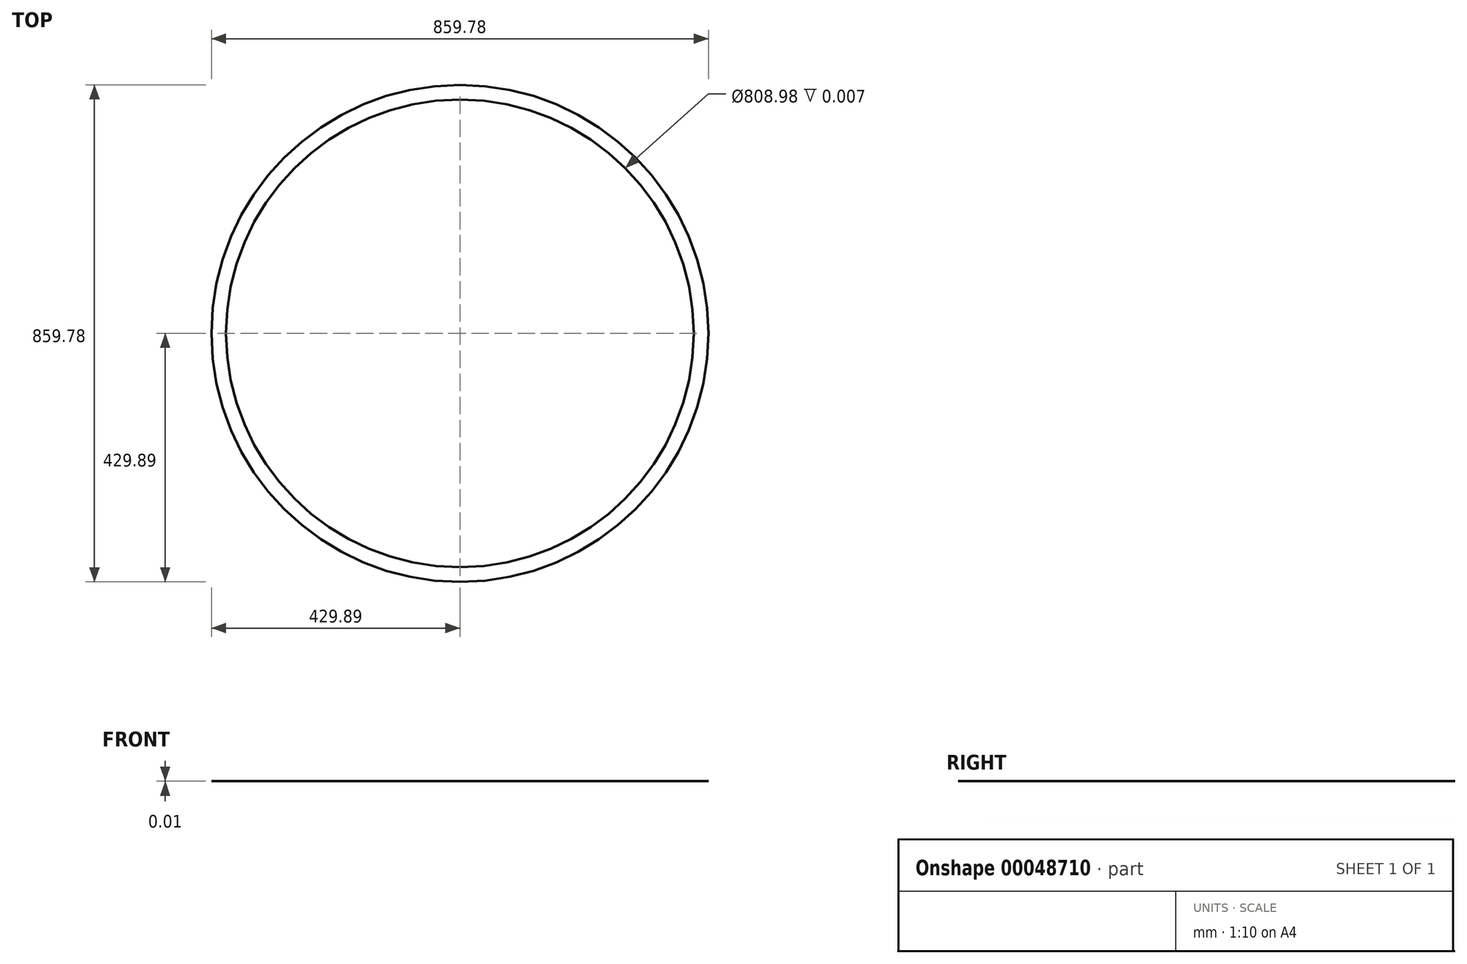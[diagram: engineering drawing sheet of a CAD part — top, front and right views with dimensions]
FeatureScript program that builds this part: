
annotation { "Feature Type Name" : "Feature", "Feature Type Description" : "" }
export const myFeature = defineFeature(function(context is Context, id is Id, definition is map)
    precondition{}
    {
        {
            var Q0;
            Q0=qCreatedBy(makeId("Top.planeOp"),FACE);
            var sketch = newSketch(context, id + "F0", { "sketchPlane" : qUnion([Q0])});
            skCircle(sketch, "E0", {"center": v(0, 0) * mm, "radius": 429.9 * mm});
            skCircle(sketch, "E1", {"center": v(0, 0) * mm, "radius": 404.5 * mm});
            skSolve(sketch);
        }
        {
            var Q0;
            Q0 = qSketchRegion(id + "F0", true);
            extrude(context, id + "F1", {"entities" : qUnion([Q0]), "depth" : 3 / 457.2 * mm});
        }
    });
